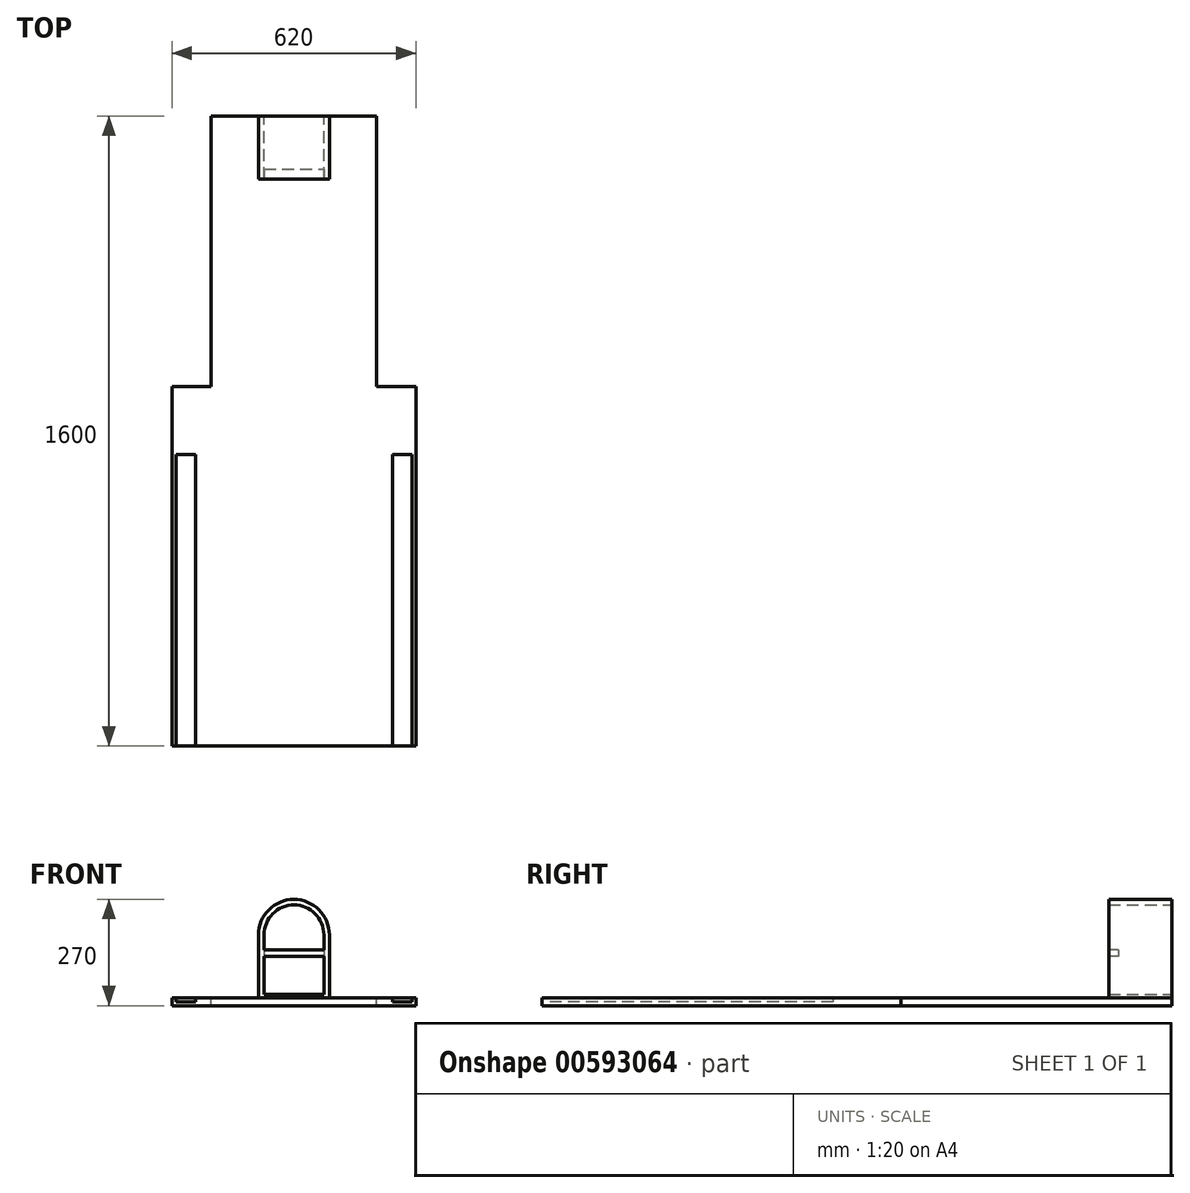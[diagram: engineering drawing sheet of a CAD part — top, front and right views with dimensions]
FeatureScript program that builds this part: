
annotation { "Feature Type Name" : "Feature", "Feature Type Description" : "" }
export const myFeature = defineFeature(function(context is Context, id is Id, definition is map)
    precondition{}
    {
        {
            var Q0;
            Q0=qCreatedBy(makeId("Top.planeOp"),FACE);
            var sketch = newSketch(context, id + "F0", { "sketchPlane" : qUnion([Q0])});
            skLineSegment(sketch, "E0.bottom", {"start": v(310, -800) * mm, "end": v(-310, -800) * mm});
            skLineSegment(sketch, "E0.top", {"start": v(310, 800) * mm, "end": v(-310, 800) * mm});
            skLineSegment(sketch, "E0.left", {"start": v(310, -800) * mm, "end": v(310, 800) * mm});
            skLineSegment(sketch, "E0.right", {"start": v(-310, -800) * mm, "end": v(-310, 800) * mm});
            skPoint(sketch, "E0.middle", {"position": v(0, 0) * mm});
            skSolve(sketch);
        }
        {
            var Q0;
            Q0 = qSketchRegion(id + "F0", true);
            extrude(context, id + "F1", {"entities" : qUnion([Q0]), "depth" : 20 * mm, "offsetDistance" : 25 * mm});
        }
        {
            var Q0;
            Q0=makeQuery(id+"F1.opExtrude","SWEPT_FACE",FACE,{"disambiguationData":[OSD([sQuery(id+"F0.wireOp",EDGE,"E0.bottom")])]});
            var sketch = newSketch(context, id + "F2", { "sketchPlane" : qUnion([Q0])});
            skLineSegment(sketch, "E1", {"start": v(0, 20) * mm, "end": v(0, 0) * mm, "construction": true});
            skLineSegment(sketch, "E2", {"start": v(0, 20) * mm, "end": v(-250, 20) * mm, "construction": true});
            skLineSegment(sketch, "E3.bottom", {"start": v(-250, 20) * mm, "end": v(-300, 20) * mm});
            skLineSegment(sketch, "E3.top", {"start": v(-250, 10) * mm, "end": v(-300, 10) * mm});
            skLineSegment(sketch, "E3.left", {"start": v(-250, 20) * mm, "end": v(-250, 10) * mm});
            skLineSegment(sketch, "E3.right", {"start": v(-300, 20) * mm, "end": v(-300, 10) * mm});
            skLineSegment(sketch, "E4.MirrorCS", {"start": v(250, 10) * mm, "end": v(300, 10) * mm});
            skLineSegment(sketch, "E5.MirrorCS", {"start": v(300, 20) * mm, "end": v(300, 10) * mm});
            skLineSegment(sketch, "E6.MirrorCS", {"start": v(250, 20) * mm, "end": v(300, 20) * mm});
            skLineSegment(sketch, "E7.MirrorCS", {"start": v(250, 20) * mm, "end": v(250, 10) * mm});
            skSolve(sketch);
        }
        {
            var Q0;
            Q0 = qSketchRegion(id + "F2", true);
            extrude(context, id + "F3", {"entities" : qUnion([Q0]), "operationType" : NewBodyOperationType.REMOVE, "oppositeDirection" : true, "depth" : 740 * mm, "offsetDistance" : 25 * mm});
        }
        {
            var Q0;
            Q0=makeQuery(id+"F1.opExtrude","CAP_FACE",FACE,{"disambiguationData":[OSD([sQuery(id+"F0.wireOp",EDGE,"E0.bottom"),sQuery(id+"F0.wireOp",EDGE,"E0.top"),sQuery(id+"F0.wireOp",EDGE,"E0.left"),sQuery(id+"F0.wireOp",EDGE,"E0.right")])],"isStart":false});
            var sketch = newSketch(context, id + "F4", { "sketchPlane" : qUnion([Q0])});
            skLineSegment(sketch, "E8", {"start": v(-310, 112.44) * mm, "end": v(-210.1, 112.44) * mm});
            skLineSegment(sketch, "E9", {"start": v(-210.1, 112.44) * mm, "end": v(-210.1, 800) * mm});
            skLineSegment(sketch, "E10", {"start": v(-210.1, 800) * mm, "end": v(-310, 800) * mm});
            skLineSegment(sketch, "E11", {"start": v(-310, 800) * mm, "end": v(-310, 112.44) * mm});
            skLineSegment(sketch, "E12", {"start": v(0, 800) * mm, "end": v(0, 0) * mm, "construction": true});
            skLineSegment(sketch, "E13.MirrorCS", {"start": v(210.1, 112.44) * mm, "end": v(210.1, 800) * mm});
            skLineSegment(sketch, "E14.MirrorCS", {"start": v(310, 112.44) * mm, "end": v(210.1, 112.44) * mm});
            skLineSegment(sketch, "E15.MirrorCS", {"start": v(310, 800) * mm, "end": v(310, 112.44) * mm});
            skLineSegment(sketch, "E16.MirrorCS", {"start": v(210.1, 800) * mm, "end": v(310, 800) * mm});
            skSolve(sketch);
        }
        {
            var Q0;
            Q0 = qSketchRegion(id + "F4", true);
            extrude(context, id + "F5", {"entities" : qUnion([Q0]), "operationType" : NewBodyOperationType.REMOVE, "endBound" : BoundingType.THROUGH_ALL, "oppositeDirection" : true, "depth" : 25 * mm, "offsetDistance" : 25 * mm});
        }
        {
            var Q0;
            Q0=makeQuery(id+"F1.opExtrude","SWEPT_FACE",FACE,{"disambiguationData":[OSD([sQuery(id+"F0.wireOp",EDGE,"E0.top")])]});
            var sketch = newSketch(context, id + "F6", { "sketchPlane" : qUnion([Q0])});
            skLineSegment(sketch, "E17", {"start": v(0, 20) * mm, "end": v(0, 270) * mm, "construction": true});
            skPoint(sketch, "E17.endSnap0", {"position": v(0, 20) * mm});
            skCircle(sketch, "E18", {"center": v(0, 180) * mm, "radius": 90 * mm});
            skLineSegment(sketch, "E19.bottom", {"start": v(0, 20) * mm, "end": v(-90, 20) * mm});
            skLineSegment(sketch, "E19.top", {"start": v(0, 180) * mm, "end": v(-90, 180) * mm});
            skLineSegment(sketch, "E19.left", {"start": v(0, 20) * mm, "end": v(0, 180) * mm});
            skLineSegment(sketch, "E19.right", {"start": v(-90, 20) * mm, "end": v(-90, 180) * mm});
            skLineSegment(sketch, "E20.bottom", {"start": v(0, 20) * mm, "end": v(90, 20) * mm});
            skLineSegment(sketch, "E20.top", {"start": v(0, 180) * mm, "end": v(90, 180) * mm});
            skLineSegment(sketch, "E20.right", {"start": v(90, 20) * mm, "end": v(90, 180) * mm});
            skSolve(sketch);
        }
        {
            var Q0;
            Q0 = qSketchRegion(id + "F6", true);
            extrude(context, id + "F7", {"entities" : qUnion([Q0]), "oppositeDirection" : true, "depth" : 160 * mm, "offsetDistance" : 25 * mm});
        }
        {
            var Q0;
            Q0=makeQuery(id+"F7.boolean.opBoolean","MERGE",FACE,{"derivedFrom":[makeQuery(id+"F1.opExtrude","SWEPT_FACE",FACE,{"disambiguationData":[OSD([sQuery(id+"F0.wireOp",EDGE,"E0.top")])]}),makeQuery(id+"F7.opExtrude","CAP_FACE",FACE,{"disambiguationData":[OSD([sQuery(id+"F6.wireOp",EDGE,"E18"),sQuery(id+"F6.wireOp",EDGE,"E19.bottom"),sQuery(id+"F6.wireOp",EDGE,"E19.right"),sQuery(id+"F6.wireOp",EDGE,"E20.bottom"),sQuery(id+"F6.wireOp",EDGE,"E20.right")])],"isStart":true})]});
            var sketch = newSketch(context, id + "F8", { "sketchPlane" : qUnion([Q0])});
            skLineSegment(sketch, "E21.0", {"start": v(-76, 28.97) * mm, "end": v(-76, 180) * mm});
            skArc(sketch, "E21.1", {"start": v(76, 180) * mm, "mid": v(0, 256) * mm, "end": v(-76, 180) * mm});
            skLineSegment(sketch, "E21.2", {"start": v(76, 28.3) * mm, "end": v(76, 180) * mm});
            skLineSegment(sketch, "E22", {"start": v(-76, 28.97) * mm, "end": v(76, 28.3) * mm});
            skSolve(sketch);
        }
        {
            var Q0;
            Q0 = qSketchRegion(id + "F8", true);
            var Q1;
            Q1=makeQuery(id+"F7.opExtrude","CAP_FACE",FACE,{"disambiguationData":[OSD([sQuery(id+"F6.wireOp",EDGE,"E18"),sQuery(id+"F6.wireOp",EDGE,"E19.bottom"),sQuery(id+"F6.wireOp",EDGE,"E19.right"),sQuery(id+"F6.wireOp",EDGE,"E20.bottom"),sQuery(id+"F6.wireOp",EDGE,"E20.right")])],"isStart":false});
            extrude(context, id + "F9", {"entities" : qUnion([Q0]), "operationType" : NewBodyOperationType.REMOVE, "endBound" : BoundingType.UP_TO_SURFACE, "oppositeDirection" : true, "depth" : 25 * mm, "endBoundEntityFace" : qUnion([Q1]), "offsetDistance" : 25 * mm});
        }
        {
            var Q0;
            Q0=makeQuery(id+"F7.opExtrude","CAP_FACE",FACE,{"disambiguationData":[OSD([sQuery(id+"F6.wireOp",EDGE,"E18"),sQuery(id+"F6.wireOp",EDGE,"E19.bottom"),sQuery(id+"F6.wireOp",EDGE,"E19.right"),sQuery(id+"F6.wireOp",EDGE,"E20.bottom"),sQuery(id+"F6.wireOp",EDGE,"E20.right")])],"isStart":false});
            var sketch = newSketch(context, id + "F10", { "sketchPlane" : qUnion([Q0])});
            skLineSegment(sketch, "E23.bottom", {"start": v(-76, 142.1) * mm, "end": v(76, 142.1) * mm});
            skLineSegment(sketch, "E23.top", {"start": v(-76, 125.32) * mm, "end": v(76, 125.32) * mm});
            skLineSegment(sketch, "E23.left", {"start": v(-76, 142.1) * mm, "end": v(-76, 125.32) * mm});
            skLineSegment(sketch, "E23.right", {"start": v(76, 142.1) * mm, "end": v(76, 125.32) * mm});
            skSolve(sketch);
        }
        {
            var Q0;
            Q0 = qSketchRegion(id + "F10", true);
            extrude(context, id + "F11", {"entities" : qUnion([Q0]), "operationType" : NewBodyOperationType.ADD, "oppositeDirection" : true, "depth" : 25 * mm, "offsetDistance" : 25 * mm});
        }
    });
